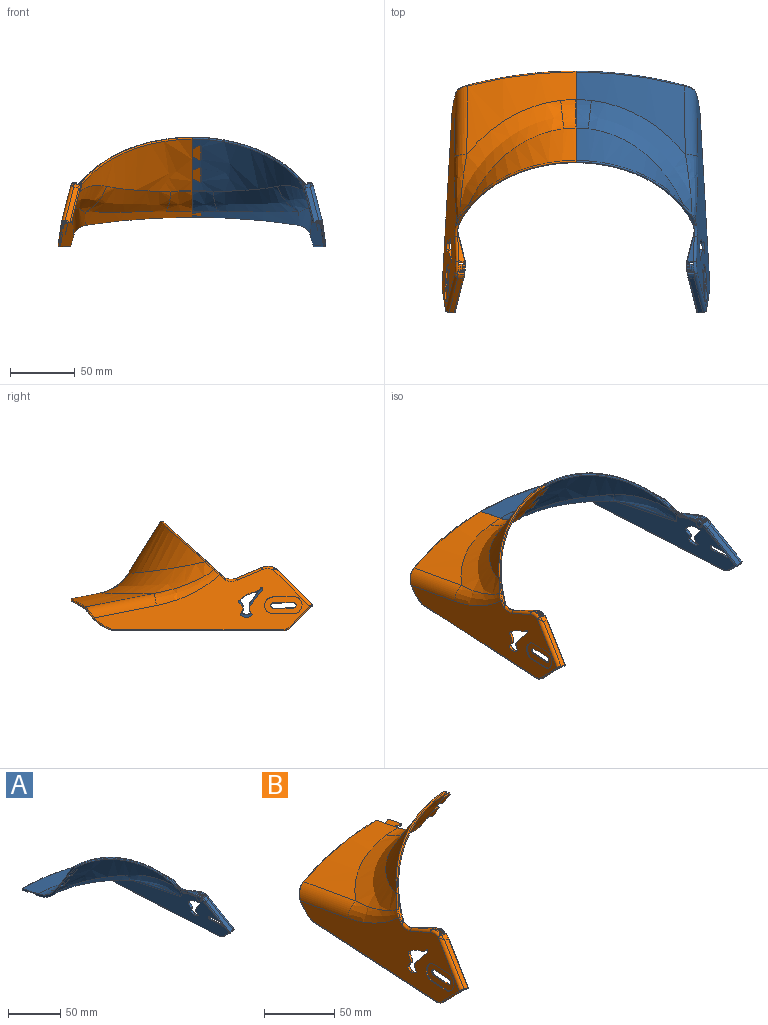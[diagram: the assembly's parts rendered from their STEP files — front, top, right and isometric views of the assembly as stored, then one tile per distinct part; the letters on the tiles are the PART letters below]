
ASSEMBLY  parts=2 mates=1
PART A: 168 faces, bbox 210.4x198x105 mm
  f0: offset ~189.87x133.43mm, area 2577.5mm2, adj f26,f28,f29,f110,f143,f152,f153,f154
  f1: plane 165.31x48.58mm, normal (-0.98,-0.06,-0.2), area 3694.6mm2, adj f26,f27,f31,f37,f39,f40,f42,f48
  f2: plane 166.79x47.25mm, normal (0.98,0.06,0.2), area 4016.3mm2, adj f24,f25,f41,f79,f80,f81,f87,f111
  f3: bspline ~10.58x3.05mm, area 1mm2, adj f7,f15,f106,f107,f108,f113
  f4: plane 5.71x4.49mm, normal (-0.98,-0.06,-0.2), area 24.1mm2, adj f61,f63,f66,f67,f98,f104
  f5: cylinder r=12mm len=5.07mm, axis (0.98,0.06,0.2), area 17.6mm2, adj f11,f82,f89,f90
  f6: cylinder r=12mm len=5.05mm, axis (0.98,0.06,0.2), area 7.2mm2, adj f50,f51,f54,f57,f59,f81
  f7: offset ~92.35x14.88mm, area 37.8mm2, adj f3,f108,f109,f110,f113,f114,f115,f143
  f8: bspline ~24.62x21.81mm, area 18.7mm2, adj f79,f83,f85,f86,f87,f93
  f9: plane 19.22x8.01mm, normal (-0.2,0.38,0.9), area 55.1mm2, adj f78,f80,f91,f92,f94
  f10: cylinder r=12mm len=4.74mm, axis (0.98,0.06,0.2), area 4.7mm2, adj f65,f66,f70,f71
  f11: plane 26.6x26.17mm, normal (-0.1,-0.71,0.69), area 143.1mm2, adj f5,f41,f88,f121
  f12: plane 16.23x15.78mm, normal (0.17,-0.73,-0.67), area 9.7mm2, adj f13,f118,f119,f121,f122,f123
  f13: cylinder r=10mm len=7.39mm, axis (0.98,0.06,0.2), area 3.3mm2, adj f12,f14,f117,f124
  f14: plane 131.72x7.92mm, normal (0.2,0.01,-0.98), area 52.8mm2, adj f13,f15,f116,f125
  f15: cylinder r=35.7mm len=19.33mm, axis (0.98,0.06,0.2), area 12.8mm2, adj f3,f14,f105,f106,f111,f112,f113
  f16: bspline ~185.25x127.06mm, area 2654mm2, adj f20,f21,f22,f25,f115,f143
  f17: bspline ~187.19x92.87mm, area 2.7mm2, adj f18,f21,f22,f23,f143
  f18: bspline ~82.94x70.61mm, area 3135.9mm2, adj f17,f20,f84,f143
  f19: offset ~191.19x97.38mm, area 10.6mm2, adj f29,f143
  f20: bspline ~111.22x98.75mm, area 2983.2mm2, adj f16,f18,f21,f24,f85
  f21: bspline ~23.12x17.69mm, area 287.5mm2, adj f16,f17,f20,f22
  f22: bspline ~22.25x15.31mm, area 6.3mm2, adj f16,f17,f21,f23
  f23: bspline ~22.24x15.3mm, area 0.3mm2, adj f17,f22,f143
  f24: bspline ~53.05x28.49mm, area 538.3mm2, adj f2,f20,f25,f86
  f25: cylinder r=12.3mm len=54.7mm, axis (0.02,-0.98,0.19), area 745.9mm2, adj f2,f16,f24,f112,f113,f114
  f26: cylinder r=12.3mm len=108.97mm, axis (0.02,-0.98,0.19), area 1180mm2, adj f0,f1,f27,f106,f107,f108,f109
  f27: bspline ~71.46x34.42mm, area 1012.5mm2, adj f1,f26,f28,f75,f76
  f28: bspline ~79.07x60.09mm, area 1935mm2, adj f0,f27,f29
  f29: bspline ~41.38x26.53mm, area 506.3mm2, adj f0,f19,f28,f143
  f30: plane 30.25x28.15mm, normal (0.11,0.69,-0.72), area 117.9mm2, adj f31,f32,f39,f88,f120
  f31: plane 7.24x5.04mm, normal (-0.05,1,-0.01), area 4.3mm2, adj f1,f30,f32,f39,f90
  f32: plane 29.87x28.17mm, normal (-0.98,-0.06,-0.2), area 33.5mm2, adj f30,f31,f88,f89,f90
  f33: plane 5.11x4.41mm, normal (-0.05,1,-0.01), area 7.8mm2, adj f46,f55,f57,f58,f67,f71,f73,f103
  f34: plane 2.48x0.64mm, normal (0.2,0,-0.98), area 1.3mm2, adj f63,f99,f101,f103
  f35: plane 5.11x4.41mm, normal (0.05,-1,0.01), area 7.8mm2, adj f47,f49,f51,f52,f61,f64,f65,f99
  f36: plane 10.72x4.01mm, normal (0.2,-0.35,-0.91), area 13.9mm2, adj f37,f40,f96
  f37: plane 6.47x3.74mm, normal (0.05,-1,0.01), area 4.7mm2, adj f1,f36,f38,f40,f92,f96
  f38: plane 1.14x1.12mm, normal (-0.98,-0.06,-0.2), area 0.5mm2, adj f37,f42,f91,f92,f96
  f39: cylinder r=2.66mm len=32.06mm, axis (-0.17,0.73,0.67), area 167.7mm2, adj f1,f30,f31,f119
  f40: cylinder r=2.66mm len=25.42mm, axis (0.02,0.93,-0.35), area 84.5mm2, adj f1,f36,f37,f97
  f41: cylinder r=2.66mm len=30.54mm, axis (0.18,-0.7,-0.69), area 162.9mm2, adj f2,f11,f82,f122
  f42: plane 24.48x11.65mm, normal (-0.96,0.16,-0.24), area 22.5mm2, adj f1,f38,f91,f94,f95,f96,f97
  f43: plane 4.49x2.23mm, normal (-0.98,-0.06,-0.2), area 7.4mm2, adj f45,f46,f47,f52,f54,f55
  f44: plane 4.49x2.23mm, normal (0.98,0.06,0.2), area 7.4mm2, adj f45,f46,f47,f64,f70,f73
  f45: plane 1.58x1.55mm, normal (-0.2,0,0.98), area 2.2mm2, adj f43,f44,f46,f47
  f46: cylinder r=2mm len=2.75mm, axis (0.98,0.06,0.2), area 5.4mm2, adj f33,f43,f44,f45,f55,f73
  f47: cylinder r=2mm len=2.95mm, axis (-0.98,-0.06,-0.2), area 5.4mm2, adj f35,f43,f44,f45,f52,f64
  f48: torus R=11.5mm, axis (0.98,0.06,0.2), area 0.8mm2, adj f1,f50,f81,f90
  f49: cylinder r=0.5mm len=3.63mm, axis (0.2,0,-0.98), area 2.7mm2, adj f1,f35,f50,f100
  f50: bspline ~1.31x1.14mm, area 0.7mm2, adj f6,f48,f49,f51,f81
  f51: cylinder r=0.5mm len=1.1mm, axis (0.98,0.06,0.2), area 0.7mm2, adj f6,f35,f50,f53
  f52: cylinder r=0.5mm len=3.39mm, axis (0.2,0,-0.98), area 2.1mm2, adj f35,f43,f47,f53
  f53: sphere r=0.5mm, area 0.2mm2, adj f51,f52,f54
  f54: torus R=11.5mm, axis (0.98,0.06,0.2), area 3.7mm2, adj f6,f43,f53,f56
  f55: cylinder r=0.5mm len=3.37mm, axis (-0.2,0,0.98), area 2.1mm2, adj f33,f43,f46,f56
  f56: sphere r=0.5mm, area 0.2mm2, adj f54,f55,f57
  f57: cylinder r=0.5mm len=1.05mm, axis (0.98,0.06,0.2), area 0.7mm2, adj f6,f33,f56,f59
  f58: cylinder r=0.5mm len=3.62mm, axis (-0.2,0,0.98), area 2.7mm2, adj f1,f33,f59,f102
  f59: bspline ~1.34x1.16mm, area 0.7mm2, adj f6,f57,f58,f60,f81
  f60: torus R=11.5mm, axis (0.98,0.06,0.2), area 0.8mm2, adj f1,f59,f81,f92
  f61: cylinder r=0.5mm len=3.63mm, axis (0.2,0,-0.98), area 2.8mm2, adj f4,f35,f62,f98
  f62: sphere r=0.5mm, area 0.2mm2, adj f61,f65,f66
  f63: cylinder r=0.5mm len=0.62mm, axis (-0.05,1,-0.01), area 0.4mm2, adj f4,f34,f98,f104
  f64: cylinder r=0.5mm len=3.37mm, axis (-0.2,0,0.98), area 2.1mm2, adj f35,f44,f47,f68
  f65: cylinder r=0.5mm len=1.1mm, axis (0.98,0.06,0.2), area 0.7mm2, adj f10,f35,f62,f68
  f66: torus R=11.5mm, axis (-0.98,-0.06,-0.2), area 3.7mm2, adj f4,f10,f62,f69
  f67: cylinder r=0.5mm len=3.62mm, axis (-0.2,0,0.98), area 2.8mm2, adj f4,f33,f69,f104
  f68: sphere r=0.5mm, area 0.4mm2, adj f64,f65,f70
  f69: sphere r=0.5mm, area 0.2mm2, adj f66,f67,f71
  f70: torus R=11.5mm, axis (-0.98,-0.06,-0.2), area 3.7mm2, adj f10,f44,f68,f72
  f71: cylinder r=0.5mm len=1.05mm, axis (0.98,0.06,0.2), area 0.7mm2, adj f10,f33,f69,f72
  f72: sphere r=0.5mm, area 0.2mm2, adj f70,f71,f73
  f73: cylinder r=0.5mm len=3.39mm, axis (0.2,0,-0.98), area 2.1mm2, adj f33,f44,f46,f72
  f74: plane 1.13x1.02mm, normal (0.17,-0.74,-0.65), area 0.2mm2, adj f1,f75,f77
  f75: plane 1.81x1.63mm, normal (-0.05,0.66,-0.75), area 0.3mm2, adj f1,f27,f74,f76,f77
  f76: plane 1.15x1mm, normal (-0.12,0.74,0.66), area 0mm2, adj f1,f27,f75,f77,f83
  f77: plane 2.56x2.53mm, normal (-0.98,-0.16,-0.08), area 3.2mm2, adj f1,f74,f75,f76
  f78: cylinder r=10mm len=2.36mm, axis (0.97,0.22,0.13), area 0.6mm2, adj f9,f79,f95
  f79: bspline ~15.48x4.82mm, area 29.4mm2, adj f2,f8,f78,f80,f87,f93
  f80: cylinder r=2mm len=20.16mm, axis (-0.02,-0.92,0.39), area 66.2mm2, adj f2,f9,f79,f81,f92
  f81: torus R=10mm, axis (0.98,0.06,0.2), area 27.9mm2, adj f2,f6,f48,f50,f59,f60,f80,f82
  f82: bspline ~5.5x3.41mm, area 7mm2, adj f5,f41,f81,f90
  f83: bspline ~98.08x51.51mm, area 189.5mm2, adj f1,f8,f76,f84,f93,f143
  f84: bspline ~86.83x36.17mm, area 155.3mm2, adj f18,f83,f85,f143
  f85: bspline ~13.3x12.03mm, area 17.6mm2, adj f8,f20,f84,f86
  f86: bspline ~6.47x5.85mm, area 8.2mm2, adj f8,f24,f85,f87
  f87: bspline ~10.72x9.42mm, area 7.7mm2, adj f2,f8,f79,f86
  f88: cylinder r=1mm len=27.24mm, axis (0.18,-0.7,-0.69), area 59mm2, adj f11,f30,f32,f89,f120,f121
  f89: torus R=11mm, axis (-0.98,-0.06,-0.2), area 7.2mm2, adj f5,f32,f88,f90
  f90: cylinder r=1mm len=5.86mm, axis (0.98,0.06,0.2), area 10.7mm2, adj f1,f5,f31,f32,f48,f81,f82,f89
  f91: cylinder r=1mm len=3.16mm, axis (-0.02,-0.92,0.39), area 2mm2, adj f9,f38,f42,f92,f94
  f92: cylinder r=1mm len=6.46mm, axis (-0.98,-0.06,-0.2), area 10.4mm2, adj f1,f9,f37,f38,f60,f80,f81,f91
  f93: bspline ~8.55x2.63mm, area 3.8mm2, adj f1,f8,f79,f83,f95
  f94: cylinder r=0.5mm len=19.02mm, axis (-0.23,-0.91,0.34), area 15.2mm2, adj f9,f42,f91,f95
  f95: bspline ~4.44x1.32mm, area 3.1mm2, adj f1,f42,f78,f93,f94
  f96: cylinder r=0.5mm len=11.11mm, axis (-0.23,-0.93,0.3), area 9.3mm2, adj f36,f37,f38,f42,f97
  f97: bspline ~13.38x7.59mm, area 8.1mm2, adj f1,f40,f42,f96
  f98: torus R=2mm, axis (-0.98,-0.06,-0.2), area 2.9mm2, adj f4,f61,f63,f99
  f99: cylinder r=2.5mm len=4.78mm, axis (-0.98,-0.06,-0.2), area 13.7mm2, adj f34,f35,f98,f100
  f100: bspline ~4.94x3mm, area 11mm2, adj f1,f49,f99,f101
  f101: cylinder r=2.5mm len=2.97mm, axis (-0.05,1,-0.01), area 2mm2, adj f1,f34,f100,f102
  f102: bspline ~4.88x3.14mm, area 11mm2, adj f1,f58,f101,f103
  f103: cylinder r=2.5mm len=5.03mm, axis (0.98,0.06,0.2), area 13.7mm2, adj f33,f34,f102,f104
  f104: torus R=2mm, axis (-0.98,-0.06,-0.2), area 2.9mm2, adj f4,f63,f67,f103
  f105: torus R=34.9mm, axis (0.98,0.06,0.2), area 19.9mm2, adj f1,f15,f106,f116
  f106: bspline ~9.2x8.28mm, area 11.7mm2, adj f3,f15,f26,f105,f107
  f107: bspline ~2.95x2.94mm, area 0.7mm2, adj f3,f26,f106,f108
  f108: bspline ~6.53x3.24mm, area 6.4mm2, adj f3,f7,f26,f107,f109
  f109: bspline ~1.13x1.12mm, area 0.3mm2, adj f7,f26,f108,f110
  f110: bspline ~86.37x12.38mm, area 104.7mm2, adj f0,f7,f109,f143
  f111: torus R=34.9mm, axis (0.98,0.06,0.2), area 21.9mm2, adj f2,f15,f112,f125
  f112: bspline ~8.65x7.06mm, area 11.2mm2, adj f15,f25,f111,f113
  f113: bspline ~2.58x2.45mm, area 0.9mm2, adj f3,f7,f15,f25,f112,f114
  f114: bspline ~8.17x4.25mm, area 7.7mm2, adj f7,f25,f113,f115
  f115: bspline ~96.06x11.86mm, area 106.8mm2, adj f7,f16,f114,f143
  f116: cylinder r=0.8mm len=131.75mm, axis (0.06,-1,0), area 165.7mm2, adj f1,f14,f105,f117
  f117: torus R=9.2mm, axis (0.98,0.06,0.2), area 10.1mm2, adj f1,f13,f116,f118
  f118: cylinder r=0.8mm len=14.81mm, axis (-0.11,-0.69,0.72), area 25.1mm2, adj f1,f12,f117,f119
  f119: torus R=3.46mm, axis (-0.17,0.73,0.67), area 5.5mm2, adj f12,f39,f118,f120,f121
  f120: cylinder r=0.8mm len=2.86mm, axis (-0.98,-0.06,-0.2), area 2.6mm2, adj f30,f88,f119,f121
  f121: cylinder r=0.8mm len=4.81mm, axis (0.98,0.06,0.2), area 4.1mm2, adj f11,f12,f88,f119,f120,f122
  f122: bspline ~3.47x2.62mm, area 4.6mm2, adj f12,f41,f121,f123
  f123: cylinder r=0.8mm len=15.81mm, axis (0.11,0.69,-0.72), area 26.4mm2, adj f2,f12,f122,f124
  f124: torus R=9.2mm, axis (0.98,0.06,0.2), area 10.1mm2, adj f2,f13,f123,f125
  f125: cylinder r=0.8mm len=131.73mm, axis (-0.06,1,0), area 165.7mm2, adj f2,f14,f111,f124
  f126: plane 15.53x1.83mm, normal (0.2,0,-0.98), area 15.5mm2, adj f2,f127,f129,f130
  f127: cylinder r=6.75mm len=13.43mm, axis (0.98,0.06,0.2), area 21.2mm2, adj f2,f126,f128,f130
  f128: plane 15.53x1.83mm, normal (-0.2,0,0.98), area 15.5mm2, adj f2,f127,f129,f130
  f129: cylinder r=6.75mm len=13.43mm, axis (0.98,0.06,0.2), area 21.2mm2, adj f2,f126,f128,f130
  f130: plane 28.95x13.41mm, normal (0.98,0.06,0.2), area 272.3mm2, adj f126,f127,f128,f129,f131,f132,f133,f134
  f131: plane 15.53x1.83mm, normal (-0.2,0,0.98), area 15.5mm2, adj f1,f130,f132,f134
  f132: cylinder r=2.12mm len=4.36mm, axis (0.98,0.06,0.2), area 6.7mm2, adj f1,f130,f131,f133
  f133: plane 15.53x1.83mm, normal (0.2,0,-0.98), area 15.5mm2, adj f1,f130,f132,f134
  f134: cylinder r=2.12mm len=4.36mm, axis (0.98,0.06,0.2), area 6.7mm2, adj f1,f130,f131,f133
  f135: cylinder r=3mm len=3.58mm, axis (0.98,0.06,0.2), area 6.9mm2, adj f1,f2,f136,f142
  f136: plane 3.96x2.99mm, normal (-0.08,-0.78,0.61), area 9.3mm2, adj f1,f2,f135,f137
  f137: cylinder r=15.17mm len=17.49mm, axis (0.98,0.06,0.2), area 41.9mm2, adj f1,f2,f136,f138
  f138: plane 11.68x8.36mm, normal (-0.16,0.81,0.57), area 28.2mm2, adj f1,f2,f137,f139
  f139: cylinder r=3mm len=3.86mm, axis (0.98,0.06,0.2), area 7.6mm2, adj f1,f2,f138,f140
  f140: plane 3.48x2.71mm, normal (0.07,0.81,-0.59), area 7.9mm2, adj f1,f2,f139,f141
  f141: cylinder r=6.43mm len=10.13mm, axis (0.98,0.06,0.2), area 23.1mm2, adj f1,f2,f140,f142
  f142: plane 3.62x2.51mm, normal (0.14,-0.88,-0.45), area 7.4mm2, adj f1,f2,f135,f141
  f143: plane 71.36x62.23mm, normal (-1,0,0), area 165.6mm2, adj f0,f7,f16,f17,f18,f19,f23,f29
  f144: plane 3.37x2.18mm, normal (0.49,0.46,-0.74), area 4.3mm2, adj f147,f160,f161
  f145: plane 9.87x6.86mm, normal (-1,0,0), area 14.2mm2, adj f147,f161,f162
  f146: plane 3.37x2.24mm, normal (0.49,-0.46,0.74), area 4.3mm2, adj f147,f162,f163
  f147: plane 11.29x7.1mm, normal (0,-0.85,-0.53), area 78.8mm2, adj f143,f144,f145,f146,f160,f161,f162,f163
  f148: plane 3.37x2.18mm, normal (0.49,0.46,-0.74), area 4.3mm2, adj f151,f164,f165
  f149: plane 9.87x6.86mm, normal (-1,0,0), area 14.2mm2, adj f151,f165,f166
  f150: plane 3.37x2.24mm, normal (0.49,-0.46,0.74), area 4.3mm2, adj f151,f166,f167
  f151: plane 11.29x7.1mm, normal (0,-0.85,-0.53), area 78.8mm2, adj f143,f148,f149,f150,f164,f165,f166,f167
  f152: plane 3.38x2.08mm, normal (0.49,-0.85,0.17), area 4.1mm2, adj f0,f155,f156,f157
  f153: plane 10.83x3.18mm, normal (-1,0,0), area 12mm2, adj f0,f155,f157,f158
  f154: plane 3.38x2.08mm, normal (0.49,0.85,-0.17), area 4.1mm2, adj f0,f155,f158,f159
  f155: plane 13.07x7.1mm, normal (0,-0.19,-0.98), area 78.8mm2, adj f143,f152,f153,f154,f156,f157,f158,f159
  f156: cylinder r=1.25mm len=1.86mm, axis (0,0.19,0.98), area 2.7mm2, adj f0,f143,f152,f155
  f157: cylinder r=1.25mm len=1.86mm, axis (0,0.19,0.98), area 2.8mm2, adj f0,f152,f153,f155
  f158: cylinder r=1.25mm len=1.86mm, axis (0,0.19,0.98), area 2.8mm2, adj f0,f153,f154,f155
  f159: cylinder r=1.25mm len=1.86mm, axis (0,0.19,0.98), area 2.7mm2, adj f0,f143,f154,f155
  f160: cylinder r=1.25mm len=1.86mm, axis (0,0.85,0.53), area 2.8mm2, adj f143,f144,f147
  f161: cylinder r=1.25mm len=1.86mm, axis (0,0.85,0.53), area 3.3mm2, adj f144,f145,f147
  f162: cylinder r=1.25mm len=1.86mm, axis (0,0.85,0.53), area 3.3mm2, adj f145,f146,f147
  f163: cylinder r=1.25mm len=1.86mm, axis (0,0.85,0.53), area 2.8mm2, adj f143,f146,f147
  f164: cylinder r=1.25mm len=1.86mm, axis (0,0.85,0.53), area 2.8mm2, adj f143,f148,f151
  f165: cylinder r=1.25mm len=1.86mm, axis (0,0.85,0.53), area 3.3mm2, adj f148,f149,f151
  f166: cylinder r=1.25mm len=1.86mm, axis (0,0.85,0.53), area 3.3mm2, adj f149,f150,f151
  f167: cylinder r=1.25mm len=1.86mm, axis (0,0.85,0.53), area 2.8mm2, adj f143,f150,f151
PART B: 178 faces, bbox 210.4x198x105 mm
  f0: plane 9.58x6.01mm, normal (0,-0.85,-0.53), area 1.6mm2, adj f159,f174,f177
  f1: plane 9.58x6.01mm, normal (0,-0.85,-0.53), area 1.6mm2, adj f160,f170,f173
  f2: bspline ~187.19x92.87mm, area 2.1mm2, adj f3,f5,f28,f148
  f3: bspline ~82.94x70.61mm, area 3135.9mm2, adj f2,f7,f27,f148
  f4: offset ~191.19x97.38mm, area 10.6mm2, adj f32,f148
  f5: bspline ~22.25x15.31mm, area 6.8mm2, adj f2,f25,f28,f148
  f6: bspline ~99.18x51.92mm, area 189.5mm2, adj f7,f8,f11,f78,f93,f148
  f7: bspline ~95.17x37.03mm, area 155.3mm2, adj f3,f6,f87,f148
  f8: plane 165.31x48.58mm, normal (0.98,-0.06,-0.2), area 3702.9mm2, adj f6,f13,f31,f35,f38,f41,f42,f44
  f9: plane 166.79x47.25mm, normal (-0.98,0.06,0.2), area 4024.6mm2, adj f29,f30,f43,f81,f82,f83,f85,f116
  f10: plane 5.71x4.49mm, normal (0.98,-0.06,-0.2), area 24.1mm2, adj f63,f65,f68,f69,f98,f104
  f11: bspline ~24.62x21.81mm, area 18.7mm2, adj f6,f81,f85,f86,f87,f93
  f12: cylinder r=12mm len=5.05mm, axis (-0.98,0.06,0.2), area 7.2mm2, adj f52,f53,f56,f59,f61,f83
  f13: bspline ~71.46x34.42mm, area 1012.5mm2, adj f8,f31,f33,f77,f78
  f14: cylinder r=12mm len=4.74mm, axis (-0.98,0.06,0.2), area 4.7mm2, adj f67,f68,f72,f73
  f15: cylinder r=12mm len=5.07mm, axis (-0.98,0.06,0.2), area 17.6mm2, adj f23,f84,f91,f92
  f16: plane 5.11x4.41mm, normal (-0.05,-1,0.01), area 7.8mm2, adj f48,f57,f59,f60,f69,f73,f75,f103
  f17: plane 5.11x4.41mm, normal (0.05,1,-0.01), area 7.8mm2, adj f49,f51,f53,f54,f63,f66,f67,f99
  f18: offset ~93.55x15.23mm, area 37.8mm2, adj f105,f106,f107,f108,f112,f113,f114,f148
  f19: cylinder r=35.7mm len=19.33mm, axis (-0.98,0.06,0.2), area 12.8mm2, adj f20,f105,f110,f111,f114,f115,f116
  f20: plane 131.72x7.92mm, normal (-0.2,0.01,-0.98), area 52.8mm2, adj f19,f21,f117,f126
  f21: cylinder r=10mm len=7.39mm, axis (-0.98,0.06,0.2), area 3.3mm2, adj f20,f22,f118,f125
  f22: plane 16.23x15.78mm, normal (-0.17,-0.73,-0.67), area 9.7mm2, adj f21,f119,f121,f122,f123,f124
  f23: plane 26.6x26.17mm, normal (0.1,-0.71,0.69), area 143.1mm2, adj f15,f43,f90,f122
  f24: plane 19.22x8.01mm, normal (0.2,0.38,0.9), area 55.1mm2, adj f80,f82,f88,f89,f95
  f25: bspline ~185.25x127.06mm, area 2654mm2, adj f5,f27,f28,f29,f112,f148
  f26: offset ~189.87x133.43mm, area 2656.3mm2, adj f31,f32,f33,f106,f148,f165
  f27: bspline ~111.22x98.75mm, area 2983.2mm2, adj f3,f25,f28,f30,f87
  f28: bspline ~23.12x17.66mm, area 287.5mm2, adj f2,f5,f25,f27
  f29: cylinder r=12.3mm len=54.7mm, axis (-0.02,-0.98,0.19), area 745.9mm2, adj f9,f25,f30,f113,f114,f115
  f30: bspline ~53.14x28.5mm, area 538.3mm2, adj f9,f27,f29,f86
  f31: cylinder r=12.3mm len=108.97mm, axis (-0.02,-0.98,0.19), area 1180mm2, adj f8,f13,f26,f107,f108,f109,f110
  f32: bspline ~41.38x26.53mm, area 506.3mm2, adj f4,f26,f33,f148
  f33: bspline ~79.07x60.09mm, area 1935mm2, adj f13,f26,f32
  f34: plane 30.25x28.15mm, normal (-0.11,0.69,-0.72), area 117.9mm2, adj f35,f36,f41,f90,f120
  f35: plane 7.24x5.04mm, normal (0.05,1,-0.01), area 4.3mm2, adj f8,f34,f36,f41,f92
  f36: plane 29.87x28.17mm, normal (0.98,-0.06,-0.2), area 33.5mm2, adj f34,f35,f90,f91,f92
  f37: plane 2.48x0.64mm, normal (-0.2,0,-0.98), area 1.3mm2, adj f65,f99,f101,f103
  f38: plane 6.47x3.74mm, normal (-0.05,-1,0.01), area 4.7mm2, adj f8,f39,f40,f42,f88,f97
  f39: plane 10.72x4.01mm, normal (-0.2,-0.35,-0.91), area 13.9mm2, adj f38,f42,f97
  f40: plane 1.14x1.12mm, normal (0.98,-0.06,-0.2), area 0.5mm2, adj f38,f44,f88,f89,f97
  f41: cylinder r=2.66mm len=32.06mm, axis (-0.17,-0.73,-0.67), area 167.7mm2, adj f8,f34,f35,f121
  f42: cylinder r=2.66mm len=25.42mm, axis (0.02,-0.93,0.35), area 84.5mm2, adj f8,f38,f39,f96
  f43: cylinder r=2.66mm len=30.54mm, axis (0.18,0.7,0.69), area 162.9mm2, adj f9,f23,f84,f123
  f44: plane 24.48x11.65mm, normal (0.96,0.16,-0.24), area 22.5mm2, adj f8,f40,f89,f94,f95,f96,f97
  f45: plane 4.49x2.23mm, normal (-0.98,0.06,0.2), area 7.4mm2, adj f47,f48,f49,f66,f72,f75
  f46: plane 4.49x2.23mm, normal (0.98,-0.06,-0.2), area 7.4mm2, adj f47,f48,f49,f54,f56,f57
  f47: plane 1.58x1.55mm, normal (0.2,0,0.98), area 2.2mm2, adj f45,f46,f48,f49
  f48: cylinder r=2mm len=2.95mm, axis (-0.98,0.06,0.2), area 5.4mm2, adj f16,f45,f46,f47,f57,f75
  f49: cylinder r=2mm len=2.75mm, axis (0.98,-0.06,-0.2), area 5.4mm2, adj f17,f45,f46,f47,f54,f66
  f50: torus R=11.5mm, axis (-0.98,0.06,0.2), area 0.8mm2, adj f8,f52,f83,f88
  f51: cylinder r=0.5mm len=3.62mm, axis (-0.2,0,-0.98), area 2.7mm2, adj f8,f17,f52,f100
  f52: bspline ~1.25x1.18mm, area 0.7mm2, adj f12,f50,f51,f53,f83
  f53: cylinder r=0.5mm len=1.05mm, axis (-0.98,0.06,0.2), area 0.7mm2, adj f12,f17,f52,f55
  f54: cylinder r=0.5mm len=3.37mm, axis (-0.2,0,-0.98), area 2.1mm2, adj f17,f46,f49,f55
  f55: sphere r=0.5mm, area 0.3mm2, adj f53,f54,f56
  f56: torus R=11.5mm, axis (0.98,-0.06,-0.2), area 3.7mm2, adj f12,f46,f55,f58
  f57: cylinder r=0.5mm len=3.39mm, axis (0.2,0,0.98), area 2.1mm2, adj f16,f46,f48,f58
  f58: sphere r=0.5mm, area 0.2mm2, adj f56,f57,f59
  f59: cylinder r=0.5mm len=1.1mm, axis (-0.98,0.06,0.2), area 0.7mm2, adj f12,f16,f58,f61
  f60: cylinder r=0.5mm len=3.63mm, axis (0.2,0,0.98), area 2.7mm2, adj f8,f16,f61,f102
  f61: bspline ~1.28x1.23mm, area 0.7mm2, adj f12,f59,f60,f62,f83
  f62: torus R=11.5mm, axis (-0.98,0.06,0.2), area 0.8mm2, adj f8,f61,f83,f92
  f63: cylinder r=0.5mm len=3.62mm, axis (-0.2,0,-0.98), area 2.8mm2, adj f10,f17,f64,f98
  f64: sphere r=0.5mm, area 0.3mm2, adj f63,f67,f68
  f65: cylinder r=0.5mm len=0.62mm, axis (-0.05,-1,0.01), area 0.4mm2, adj f10,f37,f98,f104
  f66: cylinder r=0.5mm len=3.39mm, axis (0.2,0,0.98), area 2.1mm2, adj f17,f45,f49,f70
  f67: cylinder r=0.5mm len=1.05mm, axis (-0.98,0.06,0.2), area 0.7mm2, adj f14,f17,f64,f70
  f68: torus R=11.5mm, axis (0.98,-0.06,-0.2), area 3.7mm2, adj f10,f14,f64,f71
  f69: cylinder r=0.5mm len=3.63mm, axis (0.2,0,0.98), area 2.8mm2, adj f10,f16,f71,f104
  f70: sphere r=0.5mm, area 0.2mm2, adj f66,f67,f72
  f71: sphere r=0.5mm, area 0.2mm2, adj f68,f69,f73
  f72: torus R=11.5mm, axis (-0.98,0.06,0.2), area 3.7mm2, adj f14,f45,f70,f74
  f73: cylinder r=0.5mm len=1.1mm, axis (-0.98,0.06,0.2), area 0.7mm2, adj f14,f16,f71,f74
  f74: sphere r=0.5mm, area 0.2mm2, adj f72,f73,f75
  f75: cylinder r=0.5mm len=3.37mm, axis (-0.2,0,-0.98), area 2.1mm2, adj f16,f45,f48,f74
  f76: plane 1.13x1.02mm, normal (-0.17,-0.74,-0.65), area 0.2mm2, adj f8,f77,f79
  f77: plane 1.81x1.63mm, normal (0.05,0.66,-0.75), area 0.3mm2, adj f8,f13,f76,f78,f79
  f78: plane 1.15x1mm, normal (0.12,0.74,0.66), area 0mm2, adj f6,f8,f13,f77,f79
  f79: plane 2.56x2.53mm, normal (0.98,-0.16,-0.08), area 3.2mm2, adj f8,f76,f77,f78
  f80: cylinder r=10mm len=2.36mm, axis (-0.97,0.22,0.13), area 0.6mm2, adj f24,f81,f94
  f81: bspline ~15.48x4.82mm, area 29.4mm2, adj f9,f11,f80,f82,f85,f93
  f82: cylinder r=2mm len=20.16mm, axis (-0.02,0.92,-0.39), area 66.2mm2, adj f9,f24,f81,f83,f88
  f83: torus R=10mm, axis (-0.98,0.06,0.2), area 27.9mm2, adj f9,f12,f50,f52,f61,f62,f82,f84
  f84: bspline ~5.5x3.41mm, area 7mm2, adj f15,f43,f83,f92
  f85: bspline ~10.72x9.42mm, area 7.7mm2, adj f9,f11,f81,f86
  f86: bspline ~5.92x5.34mm, area 8.2mm2, adj f11,f30,f85,f87
  f87: bspline ~13.3x12.03mm, area 17.6mm2, adj f7,f11,f27,f86
  f88: cylinder r=1mm len=6.46mm, axis (0.98,-0.06,-0.2), area 10.4mm2, adj f8,f24,f38,f40,f50,f82,f83,f89
  f89: cylinder r=1mm len=3.16mm, axis (0.02,-0.92,0.39), area 2mm2, adj f24,f40,f44,f88,f95
  f90: cylinder r=1mm len=27.24mm, axis (0.18,0.7,0.69), area 59mm2, adj f23,f34,f36,f91,f120,f122
  f91: torus R=11mm, axis (0.98,-0.06,-0.2), area 7.2mm2, adj f15,f36,f90,f92
  f92: cylinder r=1mm len=5.86mm, axis (-0.98,0.06,0.2), area 10.7mm2, adj f8,f15,f35,f36,f62,f83,f84,f91
  f93: bspline ~8.55x2.63mm, area 3.8mm2, adj f6,f8,f11,f81,f94
  f94: bspline ~4.44x1.32mm, area 3.1mm2, adj f8,f44,f80,f93,f95
  f95: cylinder r=0.5mm len=19.02mm, axis (-0.23,0.91,-0.34), area 15.2mm2, adj f24,f44,f89,f94
  f96: bspline ~13.38x7.59mm, area 8.1mm2, adj f8,f42,f44,f97
  f97: cylinder r=0.5mm len=11.11mm, axis (-0.23,0.93,-0.3), area 9.3mm2, adj f38,f39,f40,f44,f96
  f98: torus R=2mm, axis (0.98,-0.06,-0.2), area 2.9mm2, adj f10,f63,f65,f99
  f99: cylinder r=2.5mm len=5.03mm, axis (-0.98,0.06,0.2), area 13.7mm2, adj f17,f37,f98,f100
  f100: bspline ~4.88x3.14mm, area 11mm2, adj f8,f51,f99,f101
  f101: cylinder r=2.5mm len=2.97mm, axis (-0.05,-1,0.01), area 2mm2, adj f8,f37,f100,f102
  f102: bspline ~4.94x3mm, area 11mm2, adj f8,f60,f101,f103
  f103: cylinder r=2.5mm len=4.78mm, axis (0.98,-0.06,-0.2), area 13.7mm2, adj f16,f37,f102,f104
  f104: torus R=2mm, axis (0.98,-0.06,-0.2), area 2.9mm2, adj f10,f65,f69,f103
  f105: bspline ~10.58x3.05mm, area 1mm2, adj f18,f19,f108,f109,f110,f114
  f106: bspline ~89.09x12.38mm, area 104.7mm2, adj f18,f26,f107,f148
  f107: bspline ~1.13x1.13mm, area 0.3mm2, adj f18,f31,f106,f108
  f108: bspline ~6.54x3.24mm, area 6.4mm2, adj f18,f31,f105,f107,f109
  f109: bspline ~2.95x2.94mm, area 0.7mm2, adj f31,f105,f108,f110
  f110: bspline ~9.2x8.28mm, area 11.7mm2, adj f19,f31,f105,f109,f111
  f111: torus R=34.9mm, axis (-0.98,0.06,0.2), area 19.9mm2, adj f8,f19,f110,f117
  f112: bspline ~94.87x12.59mm, area 106.8mm2, adj f18,f25,f113,f148
  f113: bspline ~8.17x4.25mm, area 7.7mm2, adj f18,f29,f112,f114
  f114: bspline ~2.58x2.45mm, area 0.9mm2, adj f18,f19,f29,f105,f113,f115
  f115: bspline ~8.65x7.06mm, area 11.2mm2, adj f19,f29,f114,f116
  f116: torus R=34.9mm, axis (-0.98,0.06,0.2), area 21.9mm2, adj f9,f19,f115,f126
  f117: cylinder r=0.8mm len=131.75mm, axis (0.06,1,0), area 165.7mm2, adj f8,f20,f111,f118
  f118: torus R=9.2mm, axis (-0.98,0.06,0.2), area 10.1mm2, adj f8,f21,f117,f119
  f119: cylinder r=0.8mm len=14.81mm, axis (-0.11,0.69,-0.72), area 25.1mm2, adj f8,f22,f118,f121
  f120: cylinder r=0.8mm len=2.86mm, axis (0.98,-0.06,-0.2), area 2.6mm2, adj f34,f90,f121,f122
  f121: torus R=3.46mm, axis (-0.17,-0.73,-0.67), area 5.5mm2, adj f22,f41,f119,f120,f122
  f122: cylinder r=0.8mm len=4.81mm, axis (-0.98,0.06,0.2), area 4.1mm2, adj f22,f23,f90,f120,f121,f123
  f123: bspline ~2.88x2.21mm, area 4.6mm2, adj f22,f43,f122,f124
  f124: cylinder r=0.8mm len=15.81mm, axis (0.11,-0.69,0.72), area 26.4mm2, adj f9,f22,f123,f125
  f125: torus R=9.2mm, axis (-0.98,0.06,0.2), area 10.1mm2, adj f9,f21,f124,f126
  f126: cylinder r=0.8mm len=131.73mm, axis (-0.06,-1,0), area 165.7mm2, adj f9,f20,f116,f125
  f127: plane 15.53x1.83mm, normal (-0.2,0,-0.98), area 15.5mm2, adj f9,f128,f130,f131
  f128: cylinder r=6.75mm len=13.43mm, axis (-0.98,0.06,0.2), area 21.2mm2, adj f9,f127,f129,f131
  f129: plane 15.53x1.83mm, normal (0.2,0,0.98), area 15.5mm2, adj f9,f128,f130,f131
  f130: cylinder r=6.75mm len=13.43mm, axis (-0.98,0.06,0.2), area 21.2mm2, adj f9,f127,f129,f131
  f131: plane 28.95x13.41mm, normal (-0.98,0.06,0.2), area 272.3mm2, adj f127,f128,f129,f130,f132,f133,f134,f135
  f132: plane 15.53x1.83mm, normal (0.2,0,0.98), area 15.5mm2, adj f8,f131,f133,f135
  f133: cylinder r=2.12mm len=4.36mm, axis (-0.98,0.06,0.2), area 6.7mm2, adj f8,f131,f132,f134
  f134: plane 15.53x1.83mm, normal (-0.2,0,-0.98), area 15.5mm2, adj f8,f131,f133,f135
  f135: cylinder r=2.12mm len=4.36mm, axis (-0.98,0.06,0.2), area 6.7mm2, adj f8,f131,f132,f134
  f136: plane 3.62x2.5mm, normal (-0.14,-0.87,-0.47), area 7.5mm2, adj f8,f9,f137,f147
  f137: cylinder r=6.25mm len=9.75mm, axis (-0.98,0.06,0.2), area 22.1mm2, adj f8,f9,f136,f138
  f138: plane 3.4x2.68mm, normal (-0.07,0.82,-0.57), area 7.5mm2, adj f8,f9,f137,f139
  f139: cylinder r=3mm len=3.87mm, axis (-0.98,0.06,0.2), area 7.6mm2, adj f8,f9,f138,f140
  f140: plane 13.38x10.14mm, normal (0.16,0.79,0.59), area 33.1mm2, adj f8,f9,f139,f141
  f141: cylinder r=1.15mm len=2.31mm, axis (-0.98,0.06,0.2), area 5.6mm2, adj f8,f9,f140,f142
  f142: plane 2.66x2.3mm, normal (-0.17,-0.75,-0.64), area 6.1mm2, adj f8,f9,f141,f143
  f143: cylinder r=2mm len=2.02mm, axis (-0.98,0.06,0.2), area 2.7mm2, adj f8,f9,f142,f144
  f144: cylinder r=26.58mm len=13.59mm, axis (-0.98,0.06,0.2), area 30.4mm2, adj f8,f9,f143,f145
  f145: cylinder r=1.5mm len=2.45mm, axis (-0.98,0.06,0.2), area 4.7mm2, adj f8,f9,f144,f146
  f146: plane 3.1x2.64mm, normal (0.09,-0.75,0.65), area 7.4mm2, adj f8,f9,f145,f147
  f147: cylinder r=3mm len=3.78mm, axis (-0.98,0.06,0.2), area 7.4mm2, adj f8,f9,f136,f146
  f148: plane 71.36x62.23mm, normal (1,0,0), area 167.5mm2, adj f2,f3,f4,f5,f6,f7,f18,f25
  f149: plane 3.26x2.14mm, normal (-0.5,-0.46,0.74), area 4.2mm2, adj f152,f159,f174,f175
  f150: plane 9.73x6.74mm, normal (1,0,0), area 13.4mm2, adj f152,f158,f175,f176
  f151: plane 3.26x2.21mm, normal (-0.5,0.46,-0.74), area 4.2mm2, adj f152,f159,f176,f177
  f152: plane 11.18x7.01mm, normal (0,0.85,0.53), area 77mm2, adj f148,f149,f150,f151,f174,f175,f176,f177
  f153: plane 3.26x2.14mm, normal (-0.5,-0.46,0.74), area 4.2mm2, adj f156,f160,f170,f171
  f154: plane 9.73x6.74mm, normal (1,0,0), area 13.4mm2, adj f156,f157,f171,f172
  f155: plane 3.26x2.21mm, normal (-0.5,0.46,-0.74), area 4.2mm2, adj f156,f160,f172,f173
  f156: plane 11.18x7.01mm, normal (0,0.85,0.53), area 77mm2, adj f148,f153,f154,f155,f170,f171,f172,f173
  f157: plane 9.89x6.2mm, normal (0,-0.85,-0.53), area 1.1mm2, adj f154,f160,f171,f172
  f158: plane 9.89x6.2mm, normal (0,-0.85,-0.53), area 1.1mm2, adj f150,f159,f175,f176
  f159: plane 11.19x7.02mm, normal (-0.04,-0.85,-0.53), area 74.3mm2, adj f0,f149,f151,f158,f174,f175,f176,f177
  f160: plane 11.19x7.02mm, normal (-0.04,-0.85,-0.53), area 74.3mm2, adj f1,f153,f155,f157,f170,f171,f172,f173
  f161: plane 3.26x2.02mm, normal (-0.5,0.85,-0.17), area 3.8mm2, adj f164,f165,f166,f169
  f162: plane 10.68x3.05mm, normal (1,0,0), area 10.7mm2, adj f164,f165,f166,f167
  f163: plane 3.26x2.02mm, normal (-0.5,-0.85,0.17), area 3.8mm2, adj f164,f165,f167,f168
  f164: plane 12.94x7mm, normal (0,0.19,0.98), area 77mm2, adj f148,f161,f162,f163,f166,f167,f168,f169
  f165: plane 12.94x7mm, normal (0,-0.19,-0.98), area 77mm2, adj f26,f161,f162,f163,f166,f167,f168,f169
  f166: cylinder r=1.25mm len=1.87mm, axis (0,-0.19,-0.98), area 2.6mm2, adj f161,f162,f164,f165
  f167: cylinder r=1.25mm len=1.87mm, axis (0,-0.19,-0.98), area 2.6mm2, adj f162,f163,f164,f165
  f168: cylinder r=1.25mm len=1.87mm, axis (0,-0.19,-0.98), area 2.6mm2, adj f148,f163,f164,f165
  f169: cylinder r=1.25mm len=1.87mm, axis (0,-0.19,-0.98), area 2.6mm2, adj f148,f161,f164,f165
  f170: cylinder r=1.25mm len=1.87mm, axis (0,-0.85,-0.53), area 2.7mm2, adj f1,f148,f153,f156,f160
  f171: cylinder r=1.25mm len=1.87mm, axis (0,-0.85,-0.53), area 3.2mm2, adj f153,f154,f156,f157,f160
  f172: cylinder r=1.25mm len=1.87mm, axis (0,-0.85,-0.53), area 3.2mm2, adj f154,f155,f156,f157,f160
  f173: cylinder r=1.25mm len=1.87mm, axis (0,-0.85,-0.53), area 2.7mm2, adj f1,f148,f155,f156,f160
  f174: cylinder r=1.25mm len=1.87mm, axis (0,-0.85,-0.53), area 2.7mm2, adj f0,f148,f149,f152,f159
  f175: cylinder r=1.25mm len=1.87mm, axis (0,-0.85,-0.53), area 3.2mm2, adj f149,f150,f152,f158,f159
  f176: cylinder r=1.25mm len=1.87mm, axis (0,-0.85,-0.53), area 3.2mm2, adj f150,f151,f152,f158,f159
  f177: cylinder r=1.25mm len=1.87mm, axis (0,-0.85,-0.53), area 2.7mm2, adj f0,f148,f151,f152,f159
PLACE A t=(-60.96,-14.94,25.34)mm fixed
PLACE B t=(-60.96,-14.89,25.26)mm
MATE slider B.f148 <-> A.f143  axis (1,0,0) through (-60.96,63.1,89.31)mm
